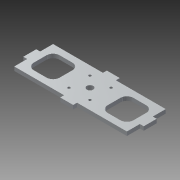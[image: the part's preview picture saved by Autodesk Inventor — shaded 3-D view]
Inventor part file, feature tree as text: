
AUTODESK INVENTOR PART (.ipt)
format: ipt  version: 2015 (Build 190159000, 159)  size: 163,328 bytes
history: native  units: mm
features: extrude x1, sketch x1
ambient origin geometry x8: Origin, YZ Plane, XZ Plane, XY Plane, X Axis, Y Axis, Z Axis, Center Point
bodies: Solid1 (feature_tree)
feature tree (2):
  extrude  "Extrusion1"  Depth=10.0mm
  sketch  "Sketch1"  dims[d0=10.0mm d1=10.0mm d2=10.0mm d3=10.0mm d4=10.0mm d5=10.0mm d6=38.5mm d7=38.5mm d8=10.0mm d9=38.5mm d11=38.5mm d12=5.0mm d13=5.0mm d15=5.0mm d16=20.0mm d17=5.0mm d18=5.0mm d19=5.0mm d20=20.0mm d21=3.0mm d23=3.0mm d24=3.0mm d25=5.0mm d26=5.0mm d27=5.0mm d28=15.0mm d30=2.0mm d32=40.0mm d34=360.0deg d36=3.0mm d37=0.0mm d38=3.0mm d39=10.0mm]
